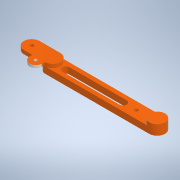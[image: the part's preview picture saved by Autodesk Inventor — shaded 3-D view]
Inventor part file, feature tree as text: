
AUTODESK INVENTOR PART (.ipt)
format: ipt  version: 2021 (Build 250183000, 183)  size: 187,904 bytes
history: native  units: mm
features: extrude x4, sketch x3, projected_geometry x3, other x1
ambient origin geometry x8: Origin, YZ Plane, XZ Plane, XY Plane, X Axis, Y Axis, Z Axis, Center Point
bodies: Body1 (feature_tree)
feature tree (11):
  other  "Sólido1"
  sketch  "Boceto1"  dims[d0=15.0mm d2=3.5mm]
  extrude  "Extrusión1"  Depth=3.5mm
  extrude  "Extrusión2"  Depth=7.0mm
  extrude  "Extrusión3"  Depth=6.0mm
  extrude  "Extrusión4"  Depth=6.0mm
  sketch  "Boceto2"  dims[d6=7.0mm d7=7.0mm]
  projected_geometry  "Contorno proyectado1"
  sketch  "Boceto3"  dims[d16=3.5mm d18=3.0mm d20=3.0mm d22=3.0mm d23=15.0mm d24=55.0mm d25=55.0mm d26=9.5mm d27=0.0mm d28=6.0mm d29=0.0mm d31=15.0mm d32=20.0mm d33=20.0mm d35=3.0mm d39=3.0mm d40=3.5mm d41=3.5mm d42=0.0mm d48=2.5mm d49=0.0mm d52=3.0mm d53=6.0mm d54=3.0mm d43=0.5mm d44=0.872665mm d45=0.5mm d46=0.872665mm]
  projected_geometry  "Contorno proyectado2"
  projected_geometry  "Contorno proyectado3"
